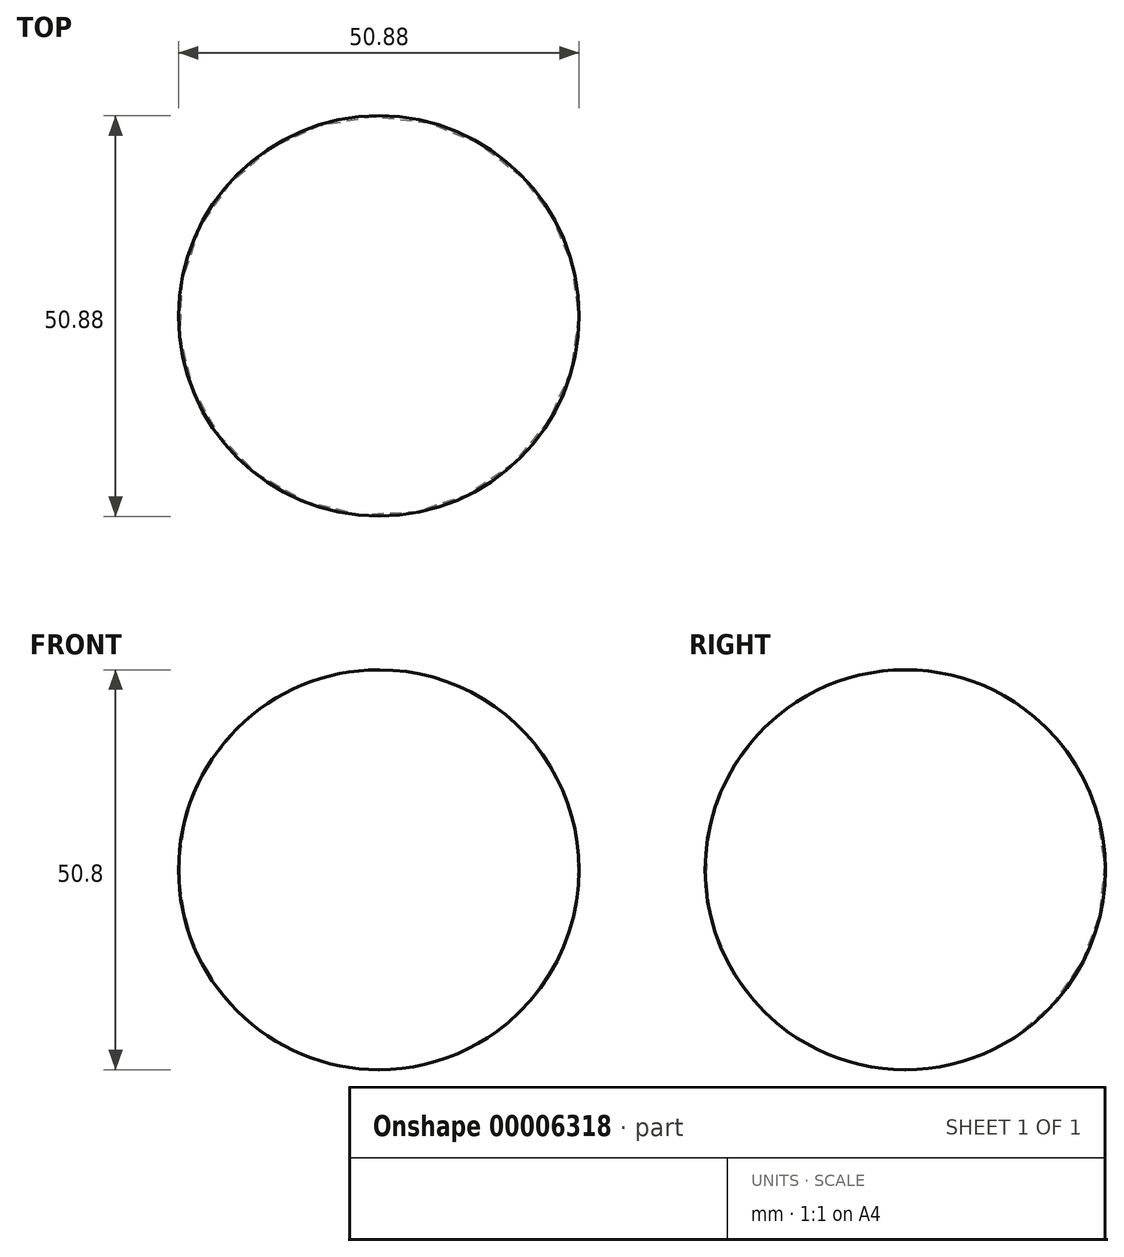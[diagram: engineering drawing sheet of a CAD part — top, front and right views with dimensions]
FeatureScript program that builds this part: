
annotation { "Feature Type Name" : "Feature", "Feature Type Description" : "" }
export const myFeature = defineFeature(function(context is Context, id is Id, definition is map)
    precondition{}
    {
        {
            var Q0;
            Q0=qCreatedBy(makeId("Front.planeOp"),FACE);
            var sketch = newSketch(context, id + "F0", { "sketchPlane" : qUnion([Q0])});
            skLineSegment(sketch, "E0", {"start": v(0, -25.4) * mm, "end": v(0, 25.4) * mm});
            skArc(sketch, "E1", {"start": v(0, -25.4) * mm, "mid": v(25.36, 0) * mm, "end": v(0, 25.4) * mm});
            skSolve(sketch);
        }
        {
            var Q0;
            Q0 = qSketchRegion(id + "F0", true);
            var Q1;
            Q1=sQuery(id+"F0.wireOp",EDGE,"E0");
            revolve(context, id + "F1", {"entities" : qUnion([Q0]), "axis" : qUnion([Q1]), "revolveType" : RevolveType.FULL});
        }
    });
